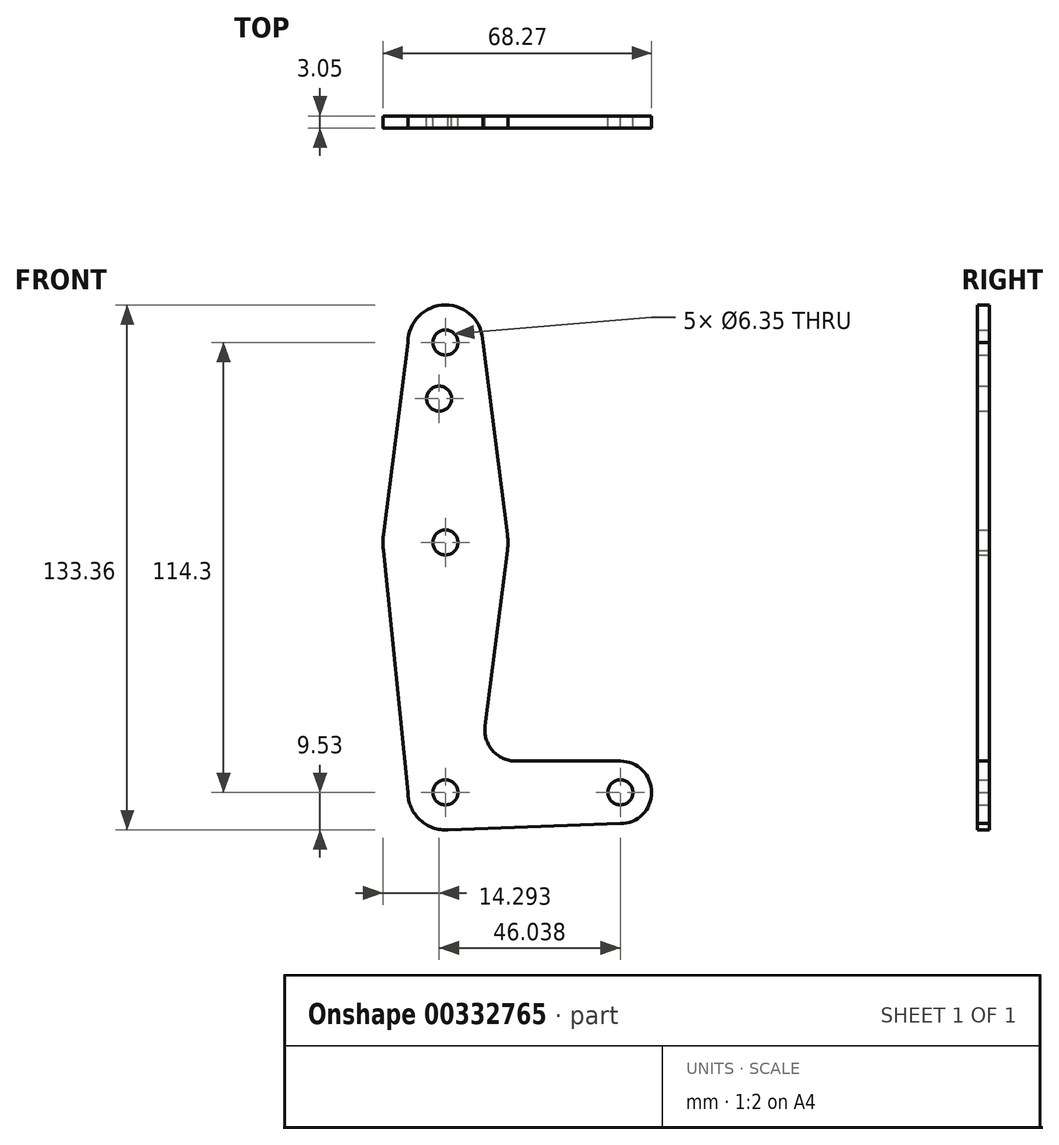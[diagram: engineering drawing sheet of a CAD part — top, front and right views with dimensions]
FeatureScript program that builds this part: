
annotation { "Feature Type Name" : "Feature", "Feature Type Description" : "" }
export const myFeature = defineFeature(function(context is Context, id is Id, definition is map)
    precondition{}
    {
        {
            var Q0;
            Q0=qCreatedBy(makeId("Front.planeOp"),FACE);
            var sketch = newSketch(context, id + "F0", { "sketchPlane" : qUnion([Q0])});
            skLineSegment(sketch, "E0", {"start": v(0, 114.3) * mm, "end": v(0, 0) * mm, "construction": true});
            skLineSegment(sketch, "E1", {"start": v(0, 0) * mm, "end": v(44.45, 0) * mm, "construction": true});
            skCircle(sketch, "E2", {"center": v(0, 114.3) * mm, "radius": 9.53 * mm});
            skCircle(sketch, "E3", {"center": v(0, 63.5) * mm, "radius": 15.88 * mm});
            skCircle(sketch, "E4", {"center": v(0, 0) * mm, "radius": 9.53 * mm});
            skCircle(sketch, "E5", {"center": v(44.45, 0) * mm, "radius": 7.94 * mm});
            skLineSegment(sketch, "E6", {"start": v(-9.53, 114.3) * mm, "end": v(-15.75, 65.5) * mm});
            skLineSegment(sketch, "E7", {"start": v(9.53, 114.3) * mm, "end": v(15.75, 65.5) * mm});
            skLineSegment(sketch, "E8", {"start": v(-9.53, 0) * mm, "end": v(-15.75, 61.5) * mm});
            skLineSegment(sketch, "E9", {"start": v(15.75, 61.5) * mm, "end": v(10.06, 16.9) * mm});
            skLineSegment(sketch, "E10", {"start": v(17.95, 7.94) * mm, "end": v(44.45, 7.94) * mm});
            skLineSegment(sketch, "E11", {"start": v(0, -9.53) * mm, "end": v(44.45, -7.94) * mm});
            skCircle(sketch, "E12", {"center": v(0, 114.3) * mm, "radius": 3.18 * mm});
            skCircle(sketch, "E13", {"center": v(0, 63.5) * mm, "radius": 3.18 * mm});
            skCircle(sketch, "E14", {"center": v(0, 0) * mm, "radius": 3.18 * mm});
            skCircle(sketch, "E15", {"center": v(44.45, 0) * mm, "radius": 3.18 * mm});
            skCircle(sketch, "E16", {"center": v(-1.59, 100.03) * mm, "radius": 3.18 * mm});
            skArc(sketch, "E17.filletArc", {"start": v(10.06, 16.9) * mm, "mid": v(11.98, 10.63) * mm, "end": v(17.95, 7.94) * mm});
            skSolve(sketch);
        }
        {
            var Q0;
            Q0 = qSketchRegion(id + "F0", true);
            extrude(context, id + "F1", {"entities" : qUnion([Q0]), "depth" : 3.05 * mm});
        }
    });
